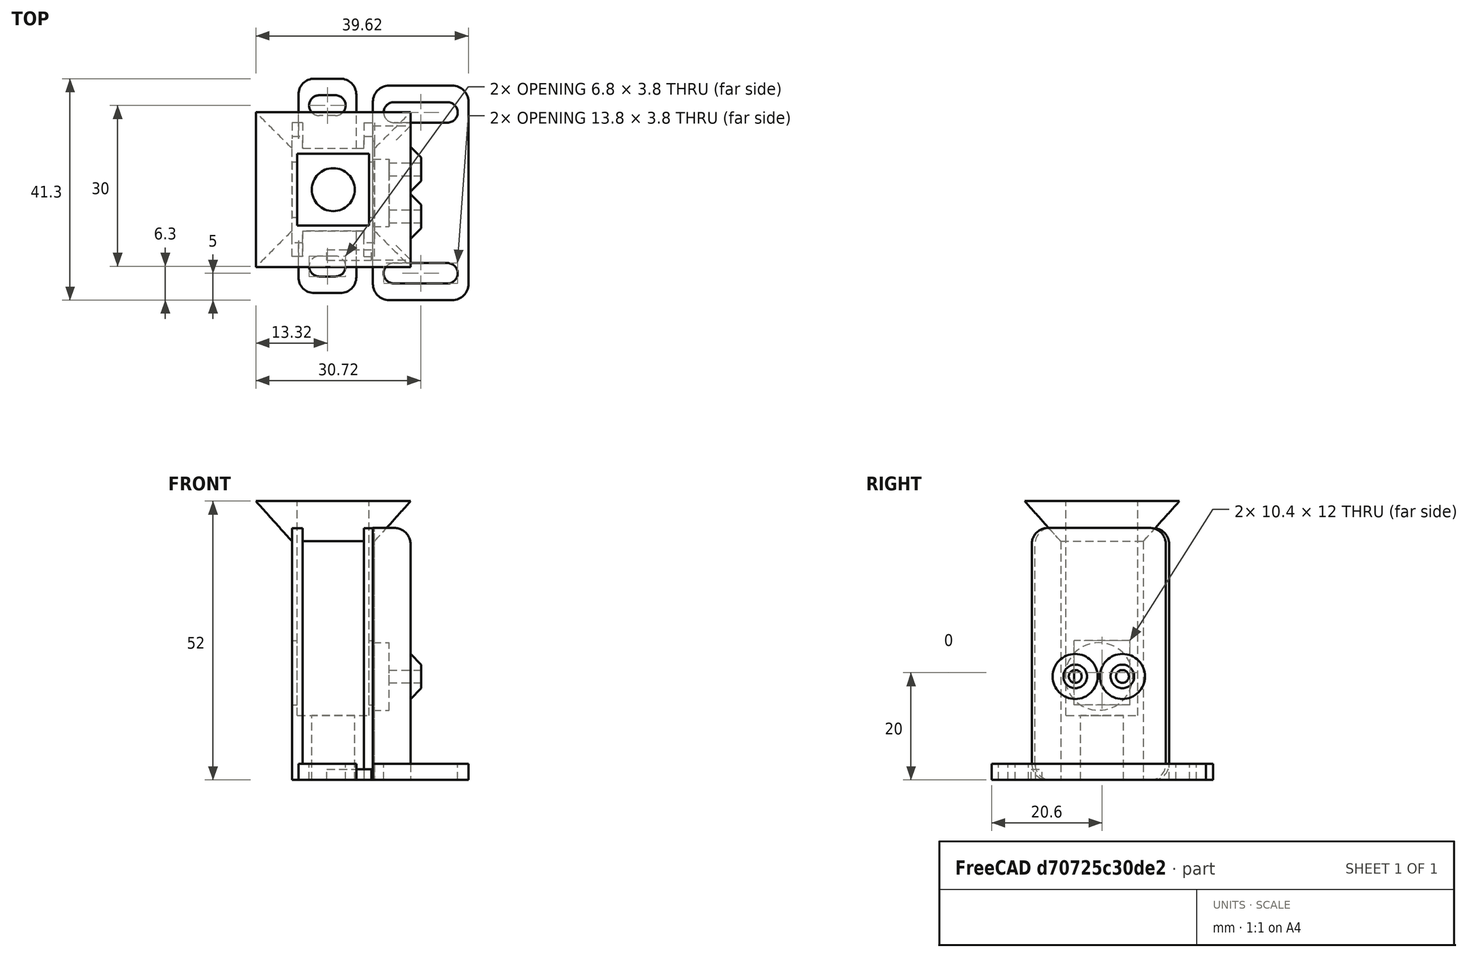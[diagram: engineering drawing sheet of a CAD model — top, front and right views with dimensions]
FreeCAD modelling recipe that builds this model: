
FCSTD DOCUMENT  (FreeCAD 0.19R23578 (Git))
Label: cuvette_box
License: FreeArt
LicenseURL: http://artlibre.org/licence/lal
objects: Part::Box×5, Part::MultiFuse×3, Part::Feature×2, Part::RegularPolygon×2, Spreadsheet::Sheet×1, Part::Fillet×1, Part::Cylinder×1, Part::Mirroring×1, Part::Loft×1, Part::Cut×1, App::Part×1
note: 17 computed .brp shape members not serialized (recipe doc carries the construction recipe); baked Part::Feature solids carry a one-line shape summary decoded from their .brp

FEATURE [Spreadsheet::Sheet] Spreadsheet  label="p"
  cells = A1=cuvette_x; B1(cuvette_x)=13.4; A2=cuvette_y; B2(cuvette_y)=13.4; A3=cuvette_h; B3(cuvette_h)=45; A4=cuvette_h_removed; B4(cuvette_h_removed)=7; A5=side_wall; B5(side_wall)=1; A6=cap_extra; B6(cap_extra)=6; A7=bottom_wall; B7(bottom_wall)=2; A8=bottom_hole_r; B8(bottom_hole_r)=4; A9=box_x; B9(box_x)==cuvette_x + 2 * side_wall; A10=box_y; B10(box_y)==cuvette_y + 2 * side_wall; A11=box_h; B11(box_h)==cuvette_h + side_wall; A12=window_wall_y; B12(window_wall_y)=25; A13=window_wall_z; B13(window_wall_z)==cuvette_h; A14=cuvette_window_y; B14(cuvette_window_y)==cuvette_y - 3; A15=cuvette_window_z; B15(cuvette_window_z)=12; A16=cuvette_window_z_off; B16(cuvette_window_z_off)=12; A17=wall; B17(wall)=2
FEATURE [Part::Box] Box  label="cuvette mockup"
  AttacherType = Attacher::AttachEngine3D
  Height = 45
  Length = 13.4
  Placement = pos=(1,1,12) rot=(0,0,1;0rad)
  Width = 13.4
  expr: .Placement.Base.x = <<p>>.side_wall
  expr: .Placement.Base.y = <<p>>.side_wall
  expr: .Placement.Base.z = <<p>>.bottom_wall + <<p>>.cuvette_window_z_off - 2
  expr: Height = <<p>>.cuvette_h
  expr: Width = <<p>>.cuvette_y
  expr: Length = <<p>>.cuvette_x
FEATURE [Part::Box] Box006  label="cuvette box"
  AttacherType = Attacher::AttachEngine3D
  Height = 52
  Length = 15.4
  Width = 15.4
  expr: Height = <<p>>.cuvette_h + <<p>>.bottom_wall + <<p>>.cuvette_window_z_off - <<p>>.cuvette_h_removed
  expr: Width = <<p>>.cuvette_y + 2 * <<p>>.side_wall
  expr: Length = <<p>>.cuvette_x + 2 * <<p>>.side_wall
FEATURE [Part::Box] Box007  label="ruler"
  AttacherType = Attacher::AttachEngine3D
  Height = 2
  Length = 8.3
  Placement = pos=(6.5,-5.5,0) rot=(0,0,1;0rad)
  Width = 2
FEATURE [Part::Box] Box008  label="cuvette window"
  AttacherType = Attacher::AttachEngine3D
  Height = 12
  Length = 50
  Placement = pos=(-25,2.5,14) rot=(0,0,1;0rad)
  Width = 10.4
  expr: .Placement.Base.y = <<p>>.side_wall + (<<p>>.cuvette_y - <<p>>.cuvette_window_y) / 2
  expr: .Placement.Base.z = <<p>>.bottom_wall + <<p>>.cuvette_window_z_off
  expr: Height = <<p>>.cuvette_window_z
  expr: Width = <<p>>.cuvette_window_y
FEATURE [Part::Box] Box009  label="cuvetter window wall"
  AttacherType = Attacher::AttachEngine3D
  Height = 47
  Length = 2
  Placement = pos=(13.4,-4.8,0) rot=(0,0,1;0rad)
  Width = 25
  expr: .Placement.Base.x = <<p>>.cuvette_x
  expr: .Placement.Base.y = -(<<p>>.window_wall_y - <<p>>.cuvette_y - 2 * <<p>>.side_wall) / 2
  expr: Length = <<p>>.wall
  expr: Height = <<p>>.window_wall_z + <<p>>.bottom_wall
  expr: Width = <<p>>.window_wall_y
FEATURE [Part::Fillet] Fillet  label="cuvetter window wall fillet"
  Base = -> Box009
  Edges = 4 edges r=3: [Edge9,Edge10,Edge11,Edge12]
FEATURE [Part::Cylinder] Cylinder  label="bottom hole"
  Angle = 360
  AttacherType = Attacher::AttachEngine3D
  Height = 50
  Placement = pos=(7.7,7.7,0) rot=(0,0,1;0rad)
  Radius = 4
  expr: .Placement.Base.y = (<<p>>.side_wall * 2 + <<p>>.cuvette_y) / 2
  expr: .Placement.Base.x = (<<p>>.side_wall * 2 + <<p>>.cuvette_x) / 2
  expr: Radius = <<p>>.bottom_hole_r
FEATURE [Part::MultiFuse] Fusion001  label="extraction fusion"
  Shapes = -> [Box,Box008,Cylinder]
FEATURE [Part::Mirroring] Part__Mirroring  label="cuvetter window wall fillet (Mirror #1)"
  Base = (7.7,0,0)
  Normal = (1,0,0)
  Source = -> Fillet
  expr: .Base.x = <<p>>.cuvette_x / 2 + <<p>>.side_wall
FEATURE [Part::MultiFuse] Fusion002  label="cuvette window wall fusion"
  Shapes = -> [Fillet,Part__Mirroring]
FEATURE [Part::Feature] Cut002001  label="attach plane y dir001"
  Placement = pos=(-1,0.8,0) rot=(0,0,1;0rad)
  shape: bbox 10.8 x 40 x 3 mm, 18 faces (baked)
FEATURE [Part::Feature] Compound002  label="photo resistor compound001"
  Placement = pos=(17.5,-5.4,0) rot=(0,0,1;0rad)
  shape: bbox 17.8 x 40 x 47 mm, 37 faces, 2 solids (baked)
FEATURE [Part::RegularPolygon] RegularPolygon  label="smaller_rect"
  AttacherType = Attacher::AttachEngine3D
  Circumradius = 7.7
  Placement = pos=(0,0,-10) rot=(0,0,1;0rad)
  Polygon = 4
  expr: Circumradius = min(<<p>>.cuvette_x; <<p>>.cuvette_y) / 2 + <<p>>.side_wall
FEATURE [Part::RegularPolygon] RegularPolygon001  label="bigger_rect"
  AttacherType = Attacher::AttachEngine3D
  Circumradius = 20.4
  Polygon = 4
  expr: Circumradius = max(<<p>>.cuvette_x; <<p>>.cuvette_y) + <<p>>.side_wall + <<p>>.cap_extra
FEATURE [Part::Loft] Loft  label="cap_loft"
  Closed = false
  MaxDegree = 5
  Placement = pos=(7.7,7.7,52) rot=(0,0,1;0.785398rad)
  Ruled = false
  Sections = -> [RegularPolygon,RegularPolygon001]
  Solid = true
  expr: .Placement.Base.y = <<p>>.cuvette_y / 2 + <<p>>.side_wall
  expr: .Placement.Base.x = <<p>>.cuvette_x / 2 + <<p>>.side_wall
  expr: .Placement.Base.z = <<p>>.cuvette_h + <<p>>.bottom_wall + <<p>>.cuvette_window_z_off - <<p>>.cuvette_h_removed
FEATURE [Part::MultiFuse] Fusion  label="cuvette fusion"
  Shapes = -> [Box006,Fusion002,Cut002001,Loft]
FEATURE [Part::Cut] Cut  label="cuvette box cut"
  Base = -> Fusion
  Tool = -> Fusion001
FEATURE [App::Part] Part  label="cuvette box part"
  Group = -> [Fusion002,Part__Mirroring,Fusion001,Cut002001,Box,Fillet,Box006,Box008,Box009,Cylinder,Fusion,Cut]
  Origin = -> Origin
